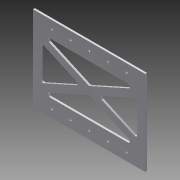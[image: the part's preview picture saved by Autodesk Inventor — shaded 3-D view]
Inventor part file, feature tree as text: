
AUTODESK INVENTOR PART (.ipt)
format: ipt  version: 2015 (Build 190159000, 159)  size: 209,920 bytes
history: native  units: in
note: dims shown in document units (in); Inventor stores cm internally (conversion verified against a paired STEP export)
features: other x6, hole x1, chamfer x1
ambient origin geometry x8: Origin, YZ Plane, XZ Plane, XY Plane, X Axis, Y Axis, Z Axis, Center Point
bodies: Solid1 (feature_tree)
feature tree (8):
  other  "profile"
  hole  "rv_holes"  [1 undecoded]
  chamfer  "Corner Round3"
  other  "profile sketch"
  other  "Plate1"
  other  "rv_hole_sketch"
  other  "cutout_sketch"
  other  "Cut2"
note: 1 required parameter value undecoded (feature->parameter linkage not recoverable at this tier; creation-order binding heuristic only, values carry confidence <= 0.55)
